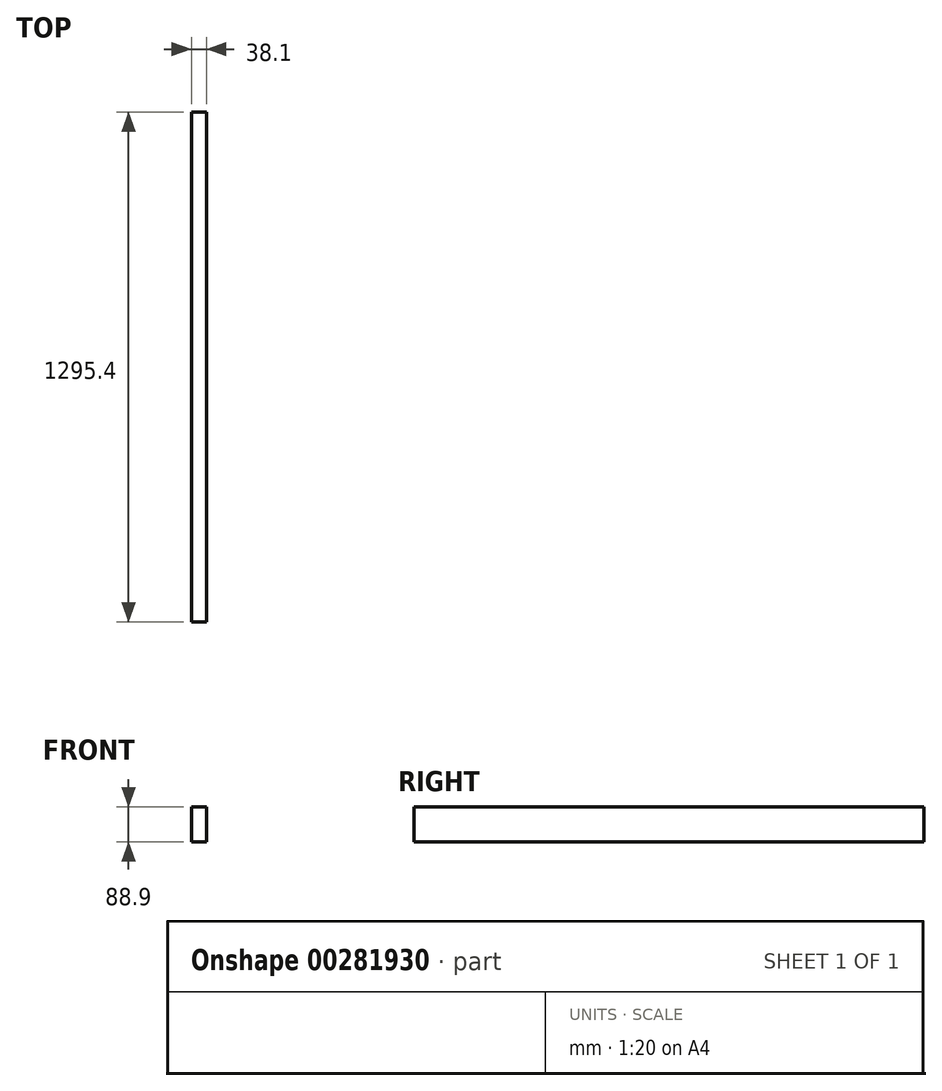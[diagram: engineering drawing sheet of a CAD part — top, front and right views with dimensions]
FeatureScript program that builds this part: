
annotation { "Feature Type Name" : "Feature", "Feature Type Description" : "" }
export const myFeature = defineFeature(function(context is Context, id is Id, definition is map)
    precondition{}
    {
        {
            var Q0;
            Q0=qCreatedBy(makeId("Front.planeOp"),FACE);
            var sketch = newSketch(context, id + "F0", { "sketchPlane" : qUnion([Q0])});
            skLineSegment(sketch, "E0.bottom", {"start": v(19.05, 44.45) * mm, "end": v(-19.05, 44.45) * mm});
            skLineSegment(sketch, "E0.top", {"start": v(19.05, -44.45) * mm, "end": v(-19.05, -44.45) * mm});
            skLineSegment(sketch, "E0.left", {"start": v(19.05, 44.45) * mm, "end": v(19.05, -44.45) * mm});
            skLineSegment(sketch, "E0.right", {"start": v(-19.05, 44.45) * mm, "end": v(-19.05, -44.45) * mm});
            skPoint(sketch, "E0.middle", {"position": v(0, 0) * mm});
            skSolve(sketch);
        }
        {
            var Q0;
            Q0=makeQuery(id+"F0.imprint","IMPRINT",FACE,{"disambiguationData":[TD([[makeQuery(id+"F0.imprint","IMPRINT",EDGE,{"derivedFrom":sQuery(id+"F0.wireOp",EDGE,"E0.bottom")}),1.0]])]});
            extrude(context, id + "F1", {"entities" : qUnion([Q0]), "depth" : 1295.4 * mm});
        }
    });
